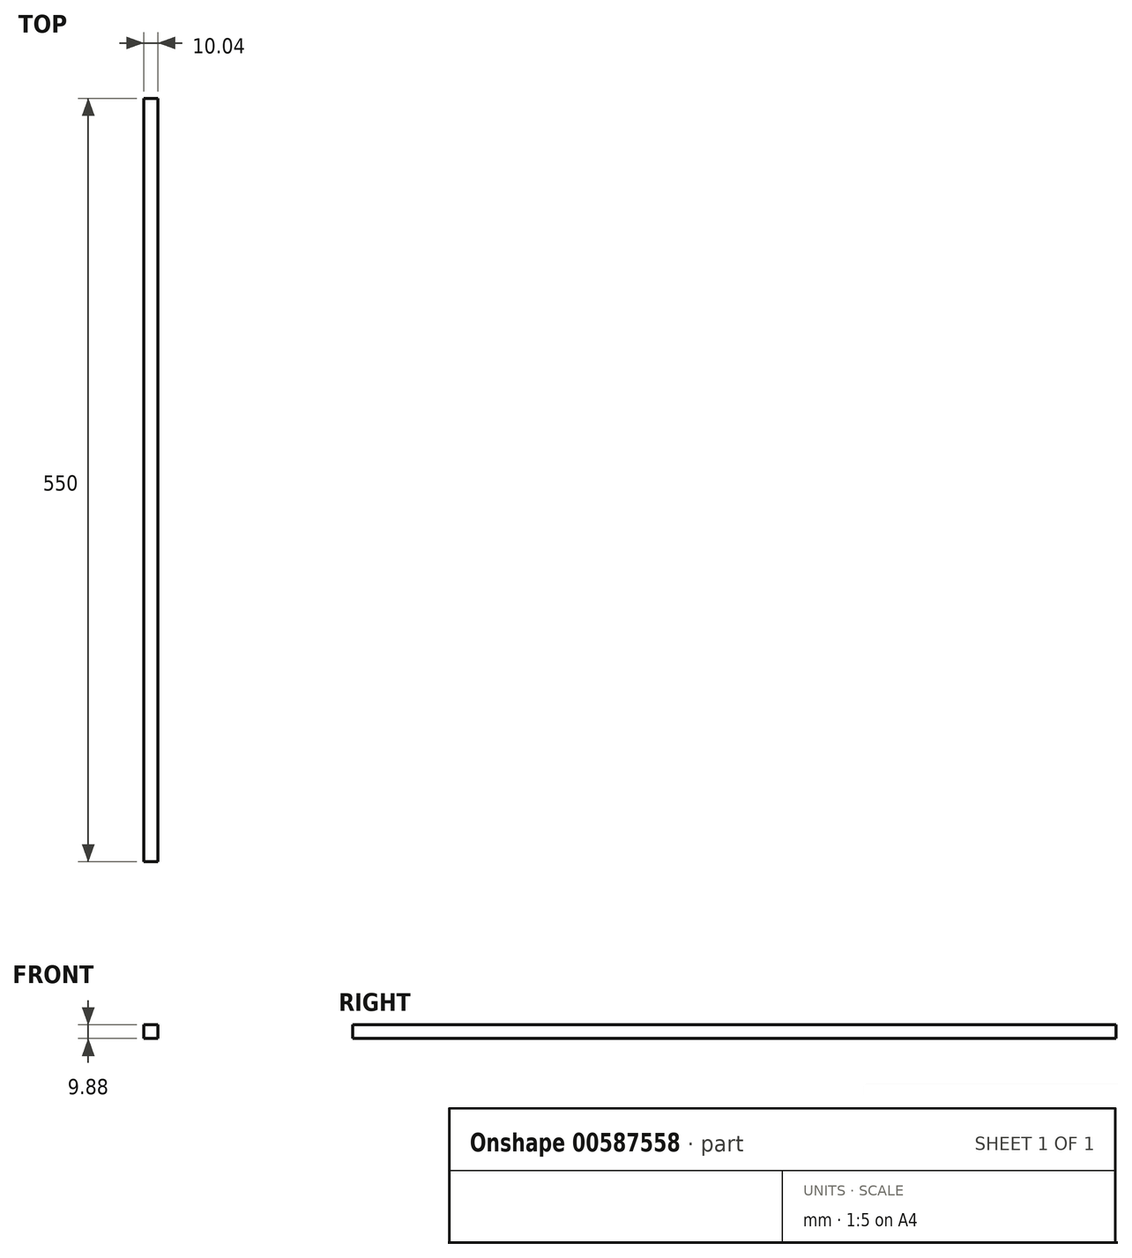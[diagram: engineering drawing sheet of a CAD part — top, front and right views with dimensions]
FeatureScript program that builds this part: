
annotation { "Feature Type Name" : "Feature", "Feature Type Description" : "" }
export const myFeature = defineFeature(function(context is Context, id is Id, definition is map)
    precondition{}
    {
        {
            var Q0;
            Q0=qCreatedBy(makeId("Front.planeOp"),FACE);
            var sketch = newSketch(context, id + "F0", { "sketchPlane" : qUnion([Q0])});
            skLineSegment(sketch, "E0.bottom", {"start": v(0, 0) * mm, "end": v(10.04, 0) * mm});
            skLineSegment(sketch, "E0.top", {"start": v(0, 9.88) * mm, "end": v(10.04, 9.88) * mm});
            skLineSegment(sketch, "E0.left", {"start": v(0, 0) * mm, "end": v(0, 9.88) * mm});
            skLineSegment(sketch, "E0.right", {"start": v(10.04, 0) * mm, "end": v(10.04, 9.88) * mm});
            skSolve(sketch);
        }
        {
            var Q0;
            Q0 = qSketchRegion(id + "F0", true);
            extrude(context, id + "F1", {"entities" : qUnion([Q0]), "depth" : 550 * mm, "offsetDistance" : 25 * mm});
        }
    });
